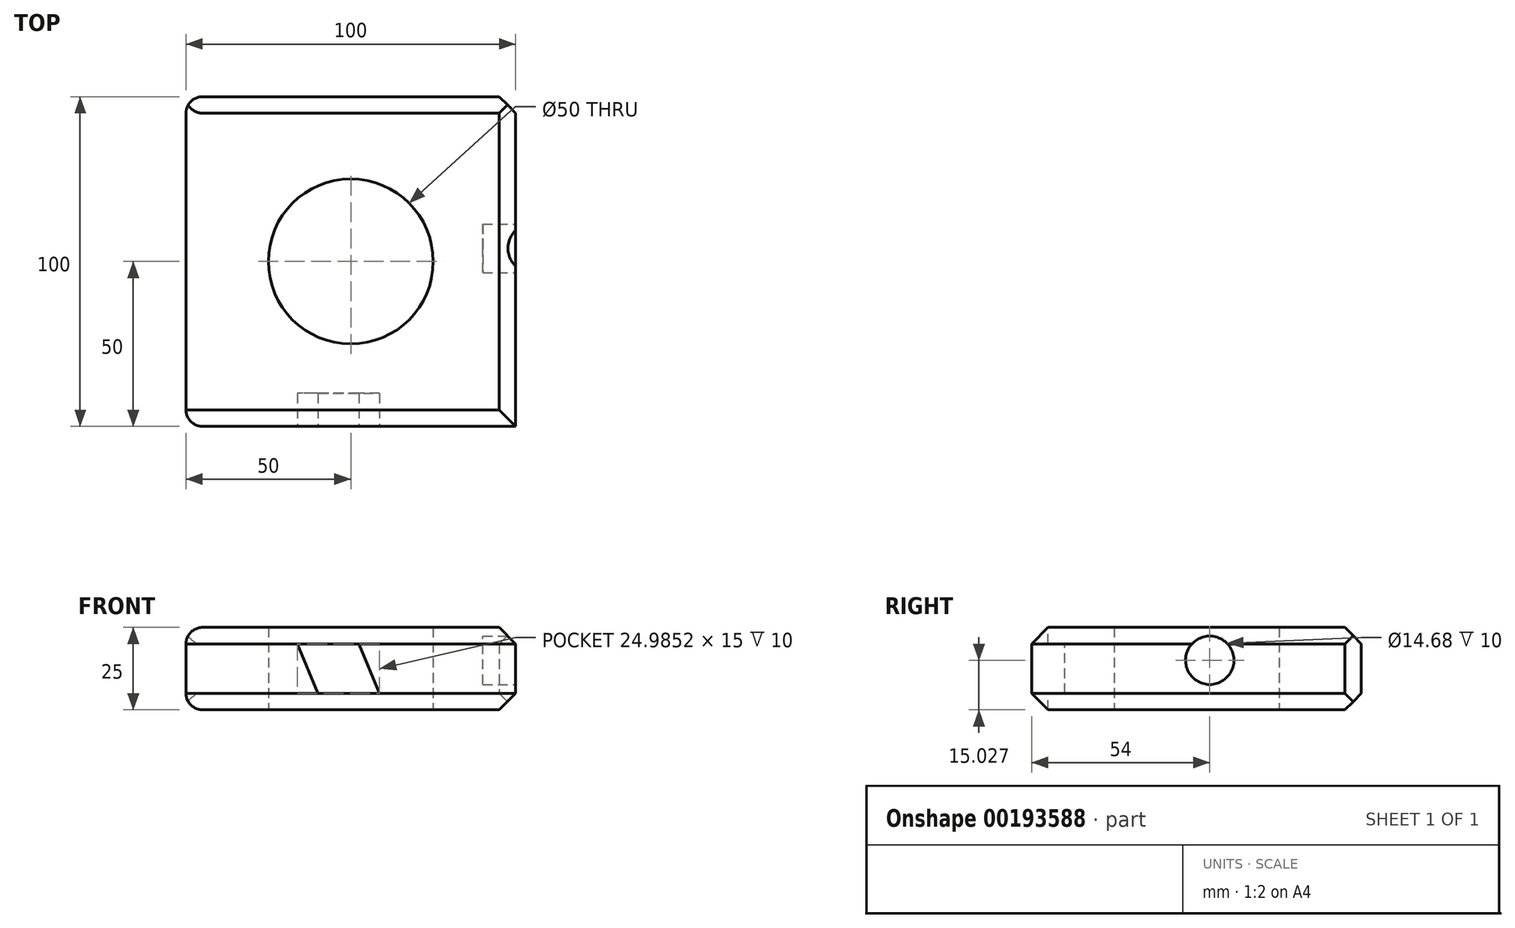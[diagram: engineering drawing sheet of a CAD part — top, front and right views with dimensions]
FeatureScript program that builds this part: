
annotation { "Feature Type Name" : "Feature", "Feature Type Description" : "" }
export const myFeature = defineFeature(function(context is Context, id is Id, definition is map)
    precondition{}
    {
        {
            var Q0;
            Q0=qCreatedBy(makeId("Top.planeOp"),FACE);
            var sketch = newSketch(context, id + "F0", { "sketchPlane" : qUnion([Q0])});
            skLineSegment(sketch, "E0.bottom", {"start": v(-50, -50) * mm, "end": v(50, -50) * mm});
            skLineSegment(sketch, "E0.top", {"start": v(-50, 50) * mm, "end": v(50, 50) * mm});
            skLineSegment(sketch, "E0.left", {"start": v(-50, -50) * mm, "end": v(-50, 50) * mm});
            skLineSegment(sketch, "E0.right", {"start": v(50, -50) * mm, "end": v(50, 50) * mm});
            skPoint(sketch, "E0.middle", {"position": v(0, 0) * mm});
            skCircle(sketch, "E1", {"center": v(0, 0) * mm, "radius": 25 * mm});
            skSolve(sketch);
        }
        {
            var Q0;
            Q0 = qSketchRegion(id + "F0", true);
            extrude(context, id + "F1", {"entities" : qUnion([Q0]), "depth" : 25 * mm});
        }
        {
            var Q0;
            Q0=makeQuery(id+"F1.opExtrude","SWEPT_FACE",FACE,{"disambiguationData":[OSD([sQuery(id+"F0.wireOp",EDGE,"E0.right")])]});
            var sketch = newSketch(context, id + "F2", { "sketchPlane" : qUnion([Q0])});
            skCircle(sketch, "E2", {"center": v(4, 15.03) * mm, "radius": 7.34 * mm});
            skSolve(sketch);
        }
        {
            var Q0;
            Q0=makeQuery(id+"F2.imprint","IMPRINT",FACE,{"disambiguationData":[TD([[makeQuery(id+"F2.imprint","IMPRINT",EDGE,{"derivedFrom":sQuery(id+"F2.wireOp",EDGE,"E2")}),1.0]])]});
            extrude(context, id + "F3", {"entities" : qUnion([Q0]), "operationType" : NewBodyOperationType.REMOVE, "oppositeDirection" : true, "depth" : 10 * mm});
        }
        {
            var Q0;
            Q0=makeQuery(id+"F1.opExtrude","CAP_EDGE",EDGE,{"disambiguationData":[OSD([sQuery(id+"F0.wireOp",EDGE,"E0.left")])],"isStart":false});
            var Q1;
            Q1=makeQuery(id+"F1.opExtrude","CAP_EDGE",EDGE,{"disambiguationData":[OSD([sQuery(id+"F0.wireOp",EDGE,"E0.left")])],"isStart":true});
            var Q2;
            Q2=makeQuery(id+"F1.opExtrude","SWEPT_FACE",FACE,{"disambiguationData":[OSD([sQuery(id+"F0.wireOp",EDGE,"E0.left")])]});
            fillet(context, id + "F4", {"entities" : qUnion([Q0, Q1, Q2]), "radius" : 5 * mm, "tangentPropagation" : true, "allowEdgeOverflow" : false});
        }
        {
            var Q0;
            {var subQ0=sQuery(id+"F0.wireOp",EDGE,"E0.left");var subQ1=sQuery(id+"F0.wireOp",EDGE,"E0.top");Q0=makeQuery(id+"Fsq3Z6YyOdC8hQQ_1.boolean.opBoolean","SPLIT",EDGE,{"disambiguationData":[TD([makeQuery(id+"F1.opExtrude","SWEPT_FACE",FACE,{"disambiguationData":[OSD([subQ0])]})])],"derivedFrom":makeQuery(id+"F1.opExtrude","CAP_EDGE",EDGE,{"disambiguationData":[OSD([subQ1])],"isStart":false})});}
            var Q1;
            {var subQ2=sQuery(id+"F0.wireOp",EDGE,"E0.left");var subQ3=sQuery(id+"F0.wireOp",EDGE,"E0.top");Q1=makeQuery(id+"Fsq3Z6YyOdC8hQQ_1.boolean.opBoolean","SPLIT",FACE,{"disambiguationData":[TD([makeQuery(id+"F1.opExtrude","SWEPT_FACE",FACE,{"disambiguationData":[OSD([subQ2])]})])],"derivedFrom":makeQuery(id+"F1.opExtrude","SWEPT_FACE",FACE,{"disambiguationData":[OSD([subQ3])]})});}
            chamfer(context, id + "F5", {"entities" : qUnion([Q0, Q1]), "width" : 5 * mm, "tangentPropagation" : true});
        }
        {
            var Q0;
            Q0=makeQuery(id+"F1.opExtrude","CAP_EDGE",EDGE,{"disambiguationData":[OSD([sQuery(id+"F0.wireOp",EDGE,"E0.bottom")])],"isStart":true});
            chamfer(context, id + "F6", {"entities" : qUnion([Q0]), "width" : 5 * mm, "tangentPropagation" : true});
        }
        {
            var Q0;
            Q0=makeQuery(id+"F1.opExtrude","CAP_EDGE",EDGE,{"disambiguationData":[OSD([sQuery(id+"F0.wireOp",EDGE,"E0.bottom")])],"isStart":false});
            chamfer(context, id + "F7", {"entities" : qUnion([Q0]), "width" : 5 * mm, "tangentPropagation" : true});
        }
        {
            var Q0;
            {var subQ0=sQuery(id+"F0.wireOp",EDGE,"E0.bottom");var subQ1=sQuery(id+"F0.wireOp",EDGE,"E0.right");Q0=makeQuery(id+"Fsq3Z6YyOdC8hQQ_1.boolean.opBoolean","SPLIT",EDGE,{"disambiguationData":[TD([makeQuery(id+"F1.opExtrude","SWEPT_FACE",FACE,{"disambiguationData":[OSD([subQ0])]})])],"derivedFrom":makeQuery(id+"F1.opExtrude","CAP_EDGE",EDGE,{"disambiguationData":[OSD([subQ1])],"isStart":false})});}
            chamfer(context, id + "F8", {"entities" : qUnion([Q0]), "width" : 5 * mm, "tangentPropagation" : true});
        }
        {
            var Q0;
            {var subQ0=sQuery(id+"F0.wireOp",EDGE,"E0.bottom");var subQ1=sQuery(id+"F0.wireOp",EDGE,"E0.right");Q0=makeQuery(id+"Fsq3Z6YyOdC8hQQ_1.boolean.opBoolean","SPLIT",EDGE,{"disambiguationData":[TD([makeQuery(id+"F1.opExtrude","SWEPT_FACE",FACE,{"disambiguationData":[OSD([subQ0])]})])],"derivedFrom":makeQuery(id+"F1.opExtrude","CAP_EDGE",EDGE,{"disambiguationData":[OSD([subQ1])],"isStart":true})});}
            chamfer(context, id + "F9", {"entities" : qUnion([Q0]), "width" : 5 * mm, "tangentPropagation" : true});
        }
        {
            var Q0;
            Q0=makeQuery(id+"F1.opExtrude","SWEPT_FACE",FACE,{"disambiguationData":[OSD([sQuery(id+"F0.wireOp",EDGE,"E0.bottom")])]});
            var sketch = newSketch(context, id + "F10", { "sketchPlane" : qUnion([Q0])});
            skLineSegment(sketch, "E3", {"start": v(8.75, 5) * mm, "end": v(2.5, 20) * mm});
            skLineSegment(sketch, "E4", {"start": v(8.75, 5) * mm, "end": v(-10, 5) * mm});
            skLineSegment(sketch, "E5", {"start": v(-10, 5) * mm, "end": v(-16.24, 20) * mm});
            skLineSegment(sketch, "E6", {"start": v(2.5, 20) * mm, "end": v(-16.24, 20) * mm});
            skSolve(sketch);
        }
        {
            var Q0;
            Q0=makeQuery(id+"F10.imprint","IMPRINT",FACE,{"disambiguationData":[TD([[makeQuery(id+"F10.imprint","IMPRINT",EDGE,{"derivedFrom":sQuery(id+"F10.wireOp",EDGE,"E3")}),1.0]])]});
            extrude(context, id + "F11", {"entities" : qUnion([Q0]), "operationType" : NewBodyOperationType.REMOVE, "oppositeDirection" : true, "depth" : 10 * mm});
        }
    });
